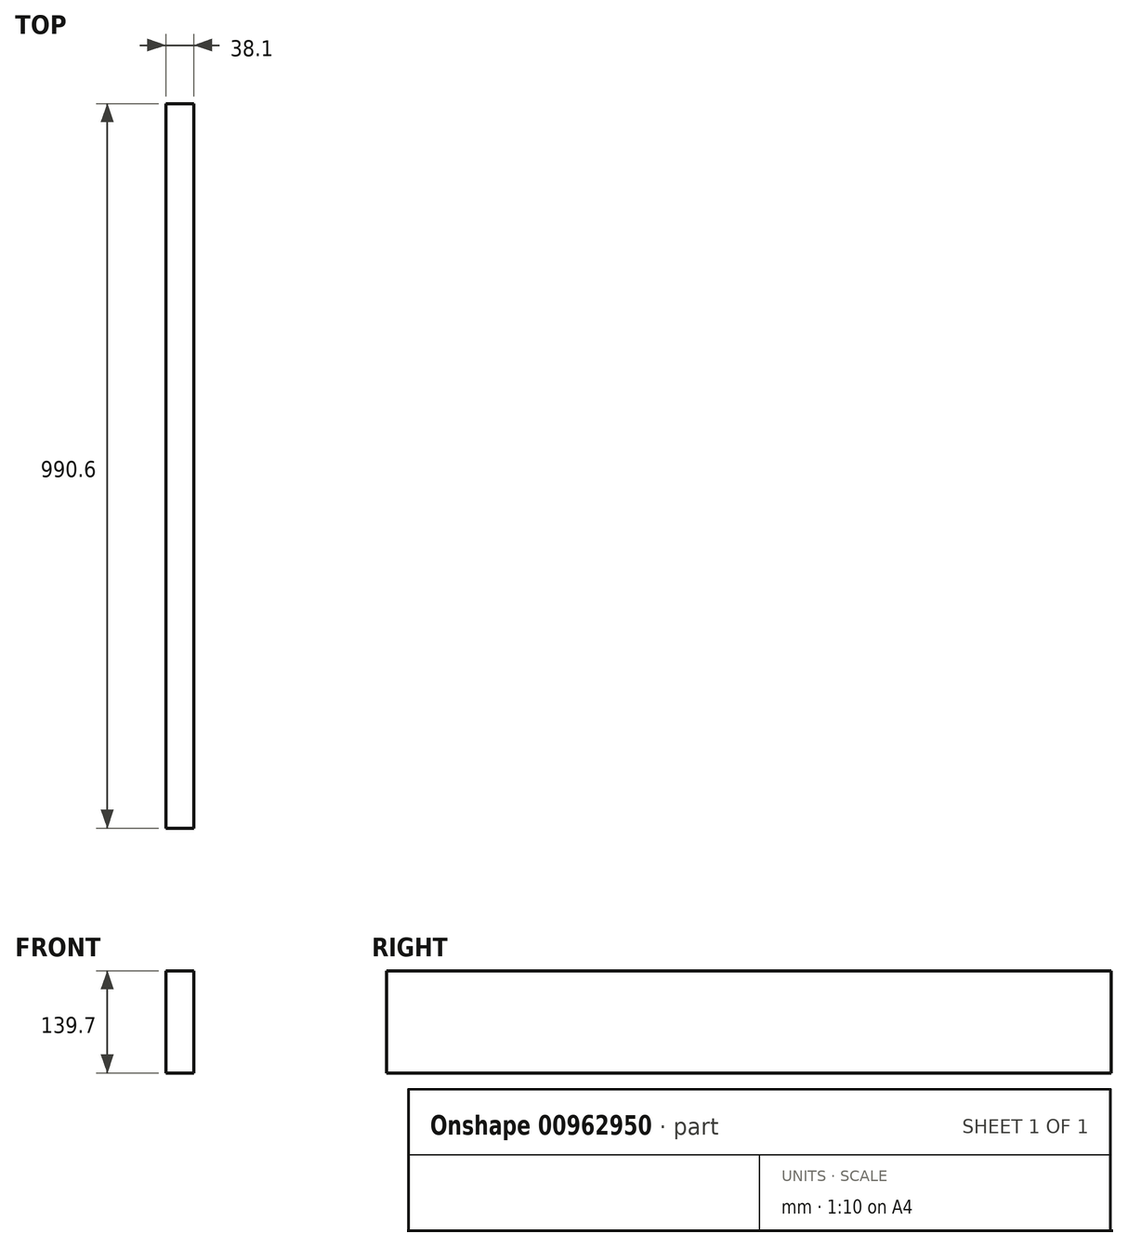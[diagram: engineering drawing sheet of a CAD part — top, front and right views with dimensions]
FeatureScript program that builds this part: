
annotation { "Feature Type Name" : "Feature", "Feature Type Description" : "" }
export const myFeature = defineFeature(function(context is Context, id is Id, definition is map)
    precondition{}
    {
        {
            var Q0;
            Q0=qCreatedBy(makeId("Front.planeOp"),FACE);
            var sketch = newSketch(context, id + "F0", { "sketchPlane" : qUnion([Q0])});
            skLineSegment(sketch, "E0.bottom", {"start": v(54.44, 121.6) * mm, "end": v(16.34, 121.6) * mm});
            skLineSegment(sketch, "E0.top", {"start": v(54.44, -18.1) * mm, "end": v(16.34, -18.1) * mm});
            skLineSegment(sketch, "E0.left", {"start": v(54.44, 121.6) * mm, "end": v(54.44, -18.1) * mm});
            skLineSegment(sketch, "E0.right", {"start": v(16.34, 121.6) * mm, "end": v(16.34, -18.1) * mm});
            skSolve(sketch);
        }
        {
            var Q0;
            Q0=makeQuery(id+"F0.imprint","IMPRINT",FACE,{"disambiguationData":[TD([[makeQuery(id+"F0.imprint","IMPRINT",EDGE,{"derivedFrom":sQuery(id+"F0.wireOp",EDGE,"E0.bottom")}),1.0]])]});
            extrude(context, id + "F1", {"entities" : qUnion([Q0]), "depth" : 990.6 * mm, "offsetDistance" : 25.4 * mm});
        }
    });
